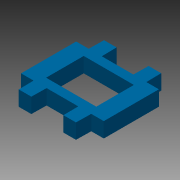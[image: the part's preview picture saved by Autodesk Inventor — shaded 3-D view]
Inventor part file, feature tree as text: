
AUTODESK INVENTOR PART (.ipt)
format: ipt  version: 2013 (Build 170138000, 138)  size: 100,864 bytes
history: native  units: mm
features: extrude x1, sketch x1
ambient origin geometry x8: Origin, YZ Plane, XZ Plane, XY Plane, X Axis, Y Axis, Z Axis, Center Point
bodies: Solid1 (feature_tree)
feature tree (2):
  extrude  "Extrusion1"  [1 undecoded]
  sketch  "Sketch1"  dims[d0=6.0mm d1=0.0mm]
note: 1 required parameter value undecoded (feature->parameter linkage not recoverable at this tier; creation-order binding heuristic only, values carry confidence <= 0.55)
